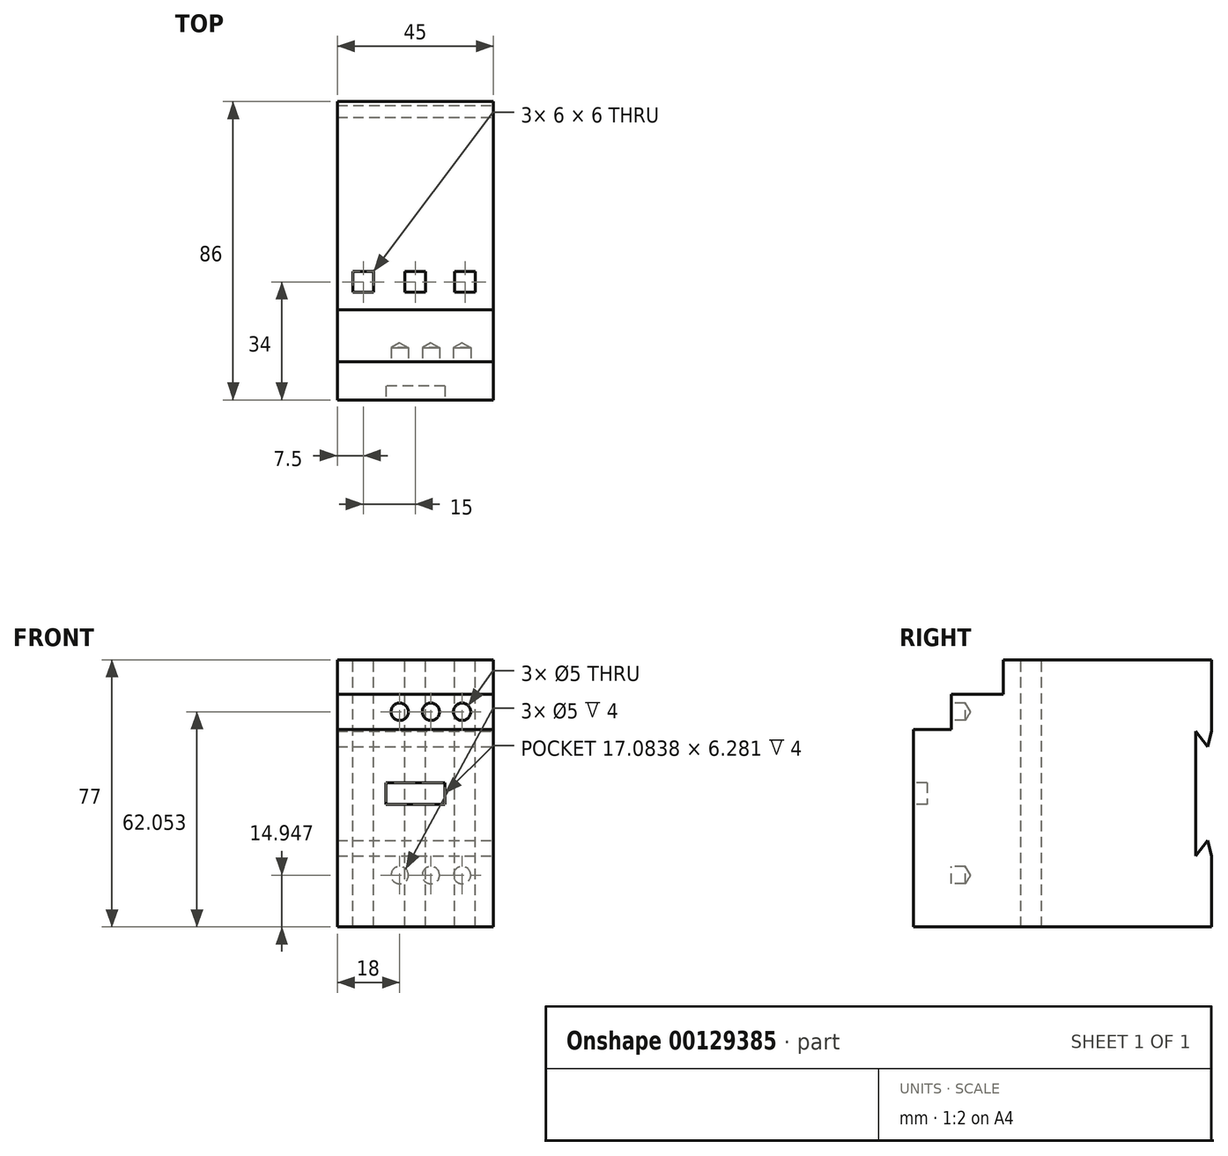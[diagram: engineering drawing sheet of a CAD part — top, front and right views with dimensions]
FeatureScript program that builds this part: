
annotation { "Feature Type Name" : "Feature", "Feature Type Description" : "" }
export const myFeature = defineFeature(function(context is Context, id is Id, definition is map)
    precondition{}
    {
        {
            var Q0;
            Q0=qCreatedBy(makeId("Front.planeOp"),FACE);
            var sketch = newSketch(context, id + "F0", { "sketchPlane" : qUnion([Q0])});
            skLineSegment(sketch, "E0.bottom", {"start": v(22.5, 38.5) * mm, "end": v(-22.5, 38.5) * mm});
            skLineSegment(sketch, "E0.top", {"start": v(22.5, -38.5) * mm, "end": v(-22.5, -38.5) * mm});
            skLineSegment(sketch, "E0.left", {"start": v(22.5, 38.5) * mm, "end": v(22.5, -38.5) * mm});
            skLineSegment(sketch, "E0.right", {"start": v(-22.5, 38.5) * mm, "end": v(-22.5, -38.5) * mm});
            skPoint(sketch, "E0.middle", {"position": v(0, 0) * mm});
            skSolve(sketch);
        }
        {
            var Q0;
            Q0=makeQuery(id+"F0.imprint","IMPRINT",FACE,{"disambiguationData":[TD([[makeQuery(id+"F0.imprint","IMPRINT",EDGE,{"derivedFrom":sQuery(id+"F0.wireOp",EDGE,"E0.bottom")}),1.0]])]});
            extrude(context, id + "F1", {"entities" : qUnion([Q0]), "depth" : 86 * mm});
        }
        {
            var Q0;
            Q0=makeQuery(id+"F1.opExtrude","SWEPT_FACE",FACE,{"disambiguationData":[OSD([sQuery(id+"F0.wireOp",EDGE,"E0.left")])]});
            var sketch = newSketch(context, id + "F2", { "sketchPlane" : qUnion([Q0])});
            skLineSegment(sketch, "E1", {"start": v(-86, 0) * mm, "end": v(-76.93, 0) * mm});
            skLineSegment(sketch, "E2", {"start": v(-86, 18.5) * mm, "end": v(12.72, 18.5) * mm});
            skLineSegment(sketch, "E3.MirrorCS", {"start": v(-86, -18.5) * mm, "end": v(12.72, -18.5) * mm});
            skLineSegment(sketch, "E4", {"start": v(-86, 38.5) * mm, "end": v(-86, -38.5) * mm});
            skPoint(sketch, "E5.orphan", {"position": v(-89.36, 18.5) * mm});
            skPoint(sketch, "E6.orphan", {"position": v(-89.36, -18.5) * mm});
            skLineSegment(sketch, "E7", {"start": v(-86, 38.5) * mm, "end": v(-75, 38.5) * mm});
            skLineSegment(sketch, "E8", {"start": v(-75, 38.5) * mm, "end": v(-75, -38.5) * mm});
            skLineSegment(sketch, "E9", {"start": v(-75, -38.5) * mm, "end": v(-60, -38.5) * mm});
            skLineSegment(sketch, "E10", {"start": v(-60, -38.5) * mm, "end": v(-60, 38.5) * mm});
            skLineSegment(sketch, "E11", {"start": v(-60, 38.5) * mm, "end": v(0, 38.5) * mm});
            skLineSegment(sketch, "E12", {"start": v(-75, 28.6) * mm, "end": v(-60, 28.6) * mm});
            skLineSegment(sketch, "E13.MirrorCS", {"start": v(-75, -28.6) * mm, "end": v(-60, -28.6) * mm});
            skLineSegment(sketch, "E14.bottom", {"start": v(-75, 38.5) * mm, "end": v(-60, 38.5) * mm});
            skLineSegment(sketch, "E14.left", {"start": v(-75, 38.5) * mm, "end": v(-75, 28.6) * mm});
            skLineSegment(sketch, "E14.right", {"start": v(-60, 38.5) * mm, "end": v(-60, 28.6) * mm});
            skLineSegment(sketch, "E15.bottom", {"start": v(-60, -28.6) * mm, "end": v(-75, -28.6) * mm});
            skLineSegment(sketch, "E15.top", {"start": v(-60, -38.5) * mm, "end": v(-75, -38.5) * mm});
            skLineSegment(sketch, "E15.left", {"start": v(-60, -28.6) * mm, "end": v(-60, -38.5) * mm});
            skLineSegment(sketch, "E15.right", {"start": v(-75, -28.6) * mm, "end": v(-75, -38.5) * mm});
            skSolve(sketch);
        }
        {
            var Q0;
            {var subQ4=sQuery(id+"F2.wireOp",EDGE,"E7");Q0=makeQuery(id+"F2.imprint","IMPRINT",FACE,{"disambiguationData":[TD([[makeQuery(id+"F2.imprint","IMPRINT",EDGE,{"derivedFrom":subQ4}),-1.0]])]});}
            var Q1;
            {var subQ0=sQuery(id+"F2.wireOp",EDGE,"E15.right");Q1=makeQuery(id+"F2.imprint","IMPRINT",FACE,{"disambiguationData":[TD([[makeQuery(id+"F2.imprint","IMPRINT",EDGE,{"derivedFrom":subQ0}),-1.0]])]});}
            var Q2;
            Q2=makeQuery(id+"F2.imprint","IMPRINT",FACE,{"disambiguationData":[TD([[makeQuery(id+"F2.imprint","IMPRINT",EDGE,{"derivedFrom":sQuery(id+"F2.wireOp",EDGE,"E14.bottom")}),-1.0]])]});
            var Q3;
            Q3=makeQuery(id+"F2.imprint","IMPRINT",FACE,{"disambiguationData":[TD([[makeQuery(id+"F2.imprint","IMPRINT",EDGE,{"derivedFrom":sQuery(id+"F2.wireOp",EDGE,"E15.bottom")}),1.0]])]});
            extrude(context, id + "F3", {"entities" : qUnion([Q0, Q1, Q2, Q3]), "operationType" : NewBodyOperationType.REMOVE, "oppositeDirection" : true, "depth" : 45 * mm});
        }
        {
            var Q0;
            Q0=makeQuery(id+"F3.boolean.opBoolean","COPY",FACE,{"derivedFrom":makeQuery(id+"F3.opExtrude","SWEPT_FACE",FACE,{"disambiguationData":[OSD([sQuery(id+"F2.wireOp",EDGE,"E12")])]})});
            var sketch = newSketch(context, id + "F4", { "sketchPlane" : qUnion([Q0])});
            skLineSegment(sketch, "E16", {"start": v(-22.5, -67.5) * mm, "end": v(-13.5, -67.5) * mm});
            skLineSegment(sketch, "E17.direction1", {"start": v(-13.5, -67.5) * mm, "end": v(-4.5, -67.5) * mm, "construction": true});
            skLineSegment(sketch, "E18.bottom", {"start": v(-15.75, -69.75) * mm, "end": v(-11.25, -69.75) * mm});
            skLineSegment(sketch, "E18.top", {"start": v(-15.75, -65.25) * mm, "end": v(-11.25, -65.25) * mm});
            skLineSegment(sketch, "E18.left", {"start": v(-15.75, -69.75) * mm, "end": v(-15.75, -65.25) * mm});
            skLineSegment(sketch, "E18.right", {"start": v(-11.25, -69.75) * mm, "end": v(-11.25, -65.25) * mm});
            skPoint(sketch, "E18.middle", {"position": v(-13.5, -67.5) * mm});
            skLineSegment(sketch, "E19.bottom", {"start": v(-6.75, -65.25) * mm, "end": v(-2.25, -65.25) * mm});
            skLineSegment(sketch, "E19.top", {"start": v(-6.75, -69.75) * mm, "end": v(-2.25, -69.75) * mm});
            skLineSegment(sketch, "E19.left", {"start": v(-6.75, -65.25) * mm, "end": v(-6.75, -69.75) * mm});
            skLineSegment(sketch, "E19.right", {"start": v(-2.25, -65.25) * mm, "end": v(-2.25, -69.75) * mm});
            skPoint(sketch, "E19.middle", {"position": v(-4.5, -67.5) * mm});
            skLineSegment(sketch, "E20.bottom", {"start": v(2.25, -65.25) * mm, "end": v(6.75, -65.25) * mm});
            skLineSegment(sketch, "E20.top", {"start": v(2.25, -69.75) * mm, "end": v(6.75, -69.75) * mm});
            skLineSegment(sketch, "E20.left", {"start": v(2.25, -65.25) * mm, "end": v(2.25, -69.75) * mm});
            skLineSegment(sketch, "E20.right", {"start": v(6.75, -65.25) * mm, "end": v(6.75, -69.75) * mm});
            skPoint(sketch, "E20.middle", {"position": v(4.5, -67.5) * mm});
            skLineSegment(sketch, "E21.bottom", {"start": v(11.25, -65.25) * mm, "end": v(15.75, -65.25) * mm});
            skLineSegment(sketch, "E21.top", {"start": v(11.25, -69.75) * mm, "end": v(15.75, -69.75) * mm});
            skLineSegment(sketch, "E21.left", {"start": v(11.25, -65.25) * mm, "end": v(11.25, -69.75) * mm});
            skLineSegment(sketch, "E21.right", {"start": v(15.75, -65.25) * mm, "end": v(15.75, -69.75) * mm});
            skPoint(sketch, "E21.middle", {"position": v(13.5, -67.5) * mm});
            skSolve(sketch);
        }
        {
            var Q0;
            Q0=makeQuery(id+"F1.opExtrude","SWEPT_FACE",FACE,{"disambiguationData":[OSD([sQuery(id+"F0.wireOp",EDGE,"E0.bottom")])]});
            var sketch = newSketch(context, id + "F5", { "sketchPlane" : qUnion([Q0])});
            skLineSegment(sketch, "E22", {"start": v(-22.5, -60) * mm, "end": v(-22.5, -52) * mm});
            skLineSegment(sketch, "E23", {"start": v(-22.5, -52) * mm, "end": v(-15, -52) * mm});
            skPoint(sketch, "E24", {"position": v(-15, -52) * mm});
            skPoint(sketch, "E25.1.0.0", {"position": v(0, -52) * mm});
            skPoint(sketch, "E25.2.0.0", {"position": v(15, -52) * mm});
            skLineSegment(sketch, "E25.direction1", {"start": v(-15, -52) * mm, "end": v(0, -52) * mm, "construction": true});
            skLineSegment(sketch, "E26.bottom", {"start": v(-12, -49) * mm, "end": v(-18, -49) * mm});
            skLineSegment(sketch, "E26.top", {"start": v(-12, -55) * mm, "end": v(-18, -55) * mm});
            skLineSegment(sketch, "E26.left", {"start": v(-12, -49) * mm, "end": v(-12, -55) * mm});
            skLineSegment(sketch, "E26.right", {"start": v(-18, -49) * mm, "end": v(-18, -55) * mm});
            skLineSegment(sketch, "E27.bottom", {"start": v(-3, -49) * mm, "end": v(3, -49) * mm});
            skLineSegment(sketch, "E27.top", {"start": v(-3, -55) * mm, "end": v(3, -55) * mm});
            skLineSegment(sketch, "E27.left", {"start": v(-3, -49) * mm, "end": v(-3, -55) * mm});
            skLineSegment(sketch, "E27.right", {"start": v(3, -49) * mm, "end": v(3, -55) * mm});
            skLineSegment(sketch, "E28.bottom", {"start": v(11.34, -49) * mm, "end": v(17.34, -49) * mm});
            skLineSegment(sketch, "E28.top", {"start": v(11.34, -55) * mm, "end": v(17.34, -55) * mm});
            skLineSegment(sketch, "E28.left", {"start": v(11.34, -49) * mm, "end": v(11.34, -55) * mm});
            skLineSegment(sketch, "E28.right", {"start": v(17.34, -49) * mm, "end": v(17.34, -55) * mm});
            skPoint(sketch, "E28.middle", {"position": v(14.34, -52) * mm});
            skSolve(sketch);
        }
        {
            var Q0;
            {var subQ3=sQuery(id+"F4.wireOp",EDGE,"E18.bottom");Q0=makeQuery(id+"F4.imprint","IMPRINT",FACE,{"disambiguationData":[TD([[makeQuery(id+"F4.imprint","IMPRINT",EDGE,{"derivedFrom":subQ3}),1.0]])]});}
            var Q1;
            Q1=makeQuery(id+"F4.imprint","IMPRINT",FACE,{"disambiguationData":[TD([[makeQuery(id+"F4.imprint","IMPRINT",EDGE,{"derivedFrom":sQuery(id+"F4.wireOp",EDGE,"E19.bottom")}),-1.0]])]});
            var Q2;
            Q2=makeQuery(id+"F4.imprint","IMPRINT",FACE,{"disambiguationData":[TD([[makeQuery(id+"F4.imprint","IMPRINT",EDGE,{"derivedFrom":sQuery(id+"F4.wireOp",EDGE,"E20.bottom")}),-1.0]])]});
            var Q3;
            Q3=makeQuery(id+"F4.imprint","IMPRINT",FACE,{"disambiguationData":[TD([[makeQuery(id+"F4.imprint","IMPRINT",EDGE,{"derivedFrom":sQuery(id+"F4.wireOp",EDGE,"E21.bottom")}),-1.0]])]});
            var Q4;
            {var subQ1=sQuery(id+"F5.wireOp",EDGE,"E26.bottom");Q4=makeQuery(id+"F5.imprint","IMPRINT",FACE,{"disambiguationData":[TD([[makeQuery(id+"F5.imprint","IMPRINT",EDGE,{"derivedFrom":subQ1}),1.0]])]});}
            var Q5;
            Q5=makeQuery(id+"F5.imprint","IMPRINT",FACE,{"disambiguationData":[TD([[makeQuery(id+"F5.imprint","IMPRINT",EDGE,{"derivedFrom":sQuery(id+"F5.wireOp",EDGE,"E27.bottom")}),-1.0]])]});
            var Q6;
            Q6=makeQuery(id+"F5.imprint","IMPRINT",FACE,{"disambiguationData":[TD([[makeQuery(id+"F5.imprint","IMPRINT",EDGE,{"derivedFrom":sQuery(id+"F5.wireOp",EDGE,"E28.bottom")}),-1.0]])]});
            var Q7;
            Q7=makeQuery(id+"F1.opExtrude","SWEPT_FACE",FACE,{"disambiguationData":[OSD([sQuery(id+"F0.wireOp",EDGE,"E0.top")])]});
            extrude(context, id + "F6", {"entities" : qUnion([Q0, Q1, Q2, Q3, Q4, Q5, Q6]), "operationType" : NewBodyOperationType.REMOVE, "endBound" : BoundingType.UP_TO_SURFACE, "oppositeDirection" : true, "endBoundEntityFace" : qUnion([Q7]), "depth" : 10 * mm});
        }
        {
            var Q0;
            Q0=makeQuery(id+"F1.opExtrude","SWEPT_FACE",FACE,{"disambiguationData":[OSD([sQuery(id+"F0.wireOp",EDGE,"E0.left")])]});
            var sketch = newSketch(context, id + "F7", { "sketchPlane" : qUnion([Q0])});
            skLineSegment(sketch, "E29.bottom", {"start": v(4.5, 18) * mm, "end": v(-4.5, 18) * mm});
            skLineSegment(sketch, "E29.top", {"start": v(4.5, -18) * mm, "end": v(-4.5, -18) * mm});
            skLineSegment(sketch, "E29.left", {"start": v(4.5, 18) * mm, "end": v(4.5, -18) * mm});
            skLineSegment(sketch, "E29.right", {"start": v(-4.5, 18) * mm, "end": v(-4.5, -18) * mm});
            skPoint(sketch, "E29.middle", {"position": v(0, 0) * mm});
            skLineSegment(sketch, "E30", {"start": v(-4.5, 18) * mm, "end": v(-1.08, 13.5) * mm});
            skLineSegment(sketch, "E31", {"start": v(-1.08, 13.5) * mm, "end": v(0, 18) * mm});
            skLineSegment(sketch, "E32.MirrorCS", {"start": v(-4.5, -18) * mm, "end": v(-1.08, -13.5) * mm});
            skLineSegment(sketch, "E33.MirrorCS", {"start": v(-1.08, -13.5) * mm, "end": v(0, -18) * mm});
            skSolve(sketch);
        }
        {
            var Q0;
            Q0=makeQuery(id+"F7.imprint","IMPRINT",FACE,{"disambiguationData":[TD([[makeQuery(id+"F7.imprint","IMPRINT",EDGE,{"derivedFrom":sQuery(id+"F7.wireOp",EDGE,"E29.right")}),1.0]])]});
            extrude(context, id + "F8", {"entities" : qUnion([Q0]), "operationType" : NewBodyOperationType.REMOVE, "oppositeDirection" : true, "depth" : 45 * mm});
        }
        {
            var Q0;
            Q0=makeQuery(id+"F1.opExtrude","CAP_FACE",FACE,{"disambiguationData":[OSD([sQuery(id+"F0.wireOp",EDGE,"E0.bottom"),sQuery(id+"F0.wireOp",EDGE,"E0.top"),sQuery(id+"F0.wireOp",EDGE,"E0.left"),sQuery(id+"F0.wireOp",EDGE,"E0.right")])],"isStart":false});
            var sketch = newSketch(context, id + "F9", { "sketchPlane" : qUnion([Q0])});
            skPoint(sketch, "E34", {"position": v(0, 0) * mm});
            skLineSegment(sketch, "E35.bottom", {"start": v(8.54, 3.14) * mm, "end": v(-8.54, 3.14) * mm});
            skLineSegment(sketch, "E35.top", {"start": v(8.54, -3.14) * mm, "end": v(-8.54, -3.14) * mm});
            skLineSegment(sketch, "E35.left", {"start": v(8.54, 3.14) * mm, "end": v(8.54, -3.14) * mm});
            skLineSegment(sketch, "E35.right", {"start": v(-8.54, 3.14) * mm, "end": v(-8.54, -3.14) * mm});
            skSolve(sketch);
        }
        {
            var Q0;
            Q0=makeQuery(id+"F9.imprint","IMPRINT",FACE,{"disambiguationData":[TD([[makeQuery(id+"F9.imprint","IMPRINT",EDGE,{"derivedFrom":sQuery(id+"F9.wireOp",EDGE,"E35.bottom")}),1.0]])]});
            extrude(context, id + "F10", {"entities" : qUnion([Q0]), "operationType" : NewBodyOperationType.REMOVE, "oppositeDirection" : true, "depth" : 4 * mm});
        }
        {
            var Q0;
            {var subQ0=sQuery(id+"F2.wireOp",EDGE,"E8");Q0=makeQuery(id+"F3.boolean.opBoolean","COPY",FACE,{"derivedFrom":makeQuery(id+"F3.opExtrude","SWEPT_FACE",FACE,{"disambiguationData":[OSD([subQ0]),TDD([makeQuery(id+"F2.imprint","IMPRINT",EDGE,{"disambiguationData":[TD([[makeQuery(id+"F2.imprint","INTERSECT",VERTEX,{"derivedFrom":[sQuery(id+"F2.wireOp",EDGE,"E2"),subQ0]}),1.0]])],"derivedFrom":subQ0})])]})});}
            var sketch = newSketch(context, id + "F11", { "sketchPlane" : qUnion([Q0])});
            skPoint(sketch, "E36", {"position": v(-13.5, 23.55) * mm});
            skPoint(sketch, "E36.positionSnap0", {"position": v(-22.5, 23.55) * mm});
            skPoint(sketch, "E37.1.0.0", {"position": v(-4.5, 23.55) * mm});
            skPoint(sketch, "E37.2.0.0", {"position": v(4.5, 23.55) * mm});
            skPoint(sketch, "E37.3.0.0", {"position": v(13.5, 23.55) * mm});
            skLineSegment(sketch, "E37.direction1", {"start": v(-13.5, 23.55) * mm, "end": v(-4.5, 23.55) * mm, "construction": true});
            skSolve(sketch);
        }
        {
            var Q0;
            Q0=makeQuery(id+"F3.boolean.opBoolean","COPY",FACE,{"derivedFrom":makeQuery(id+"F3.opExtrude","SWEPT_FACE",FACE,{"disambiguationData":[OSD([sQuery(id+"F2.wireOp",EDGE,"E14.right")])]})});
            var sketch = newSketch(context, id + "F12", { "sketchPlane" : qUnion([Q0])});
            skPoint(sketch, "E38", {"position": v(-22.5, 33.55) * mm});
            skPoint(sketch, "E39", {"position": v(-15, 33.55) * mm});
            skPoint(sketch, "E40.1.0.0", {"position": v(0, 33.55) * mm});
            skPoint(sketch, "E40.2.0.0", {"position": v(15, 33.55) * mm});
            skLineSegment(sketch, "E40.direction1", {"start": v(-15, 33.55) * mm, "end": v(0, 33.55) * mm, "construction": true});
            skSolve(sketch);
        }
        {
            var Q0;
            {var subQ0=sQuery(id+"F2.wireOp",EDGE,"E8");Q0=makeQuery(id+"F3.boolean.opBoolean","COPY",FACE,{"derivedFrom":makeQuery(id+"F3.opExtrude","SWEPT_FACE",FACE,{"disambiguationData":[OSD([subQ0]),TDD([makeQuery(id+"F2.imprint","IMPRINT",EDGE,{"disambiguationData":[TD([[makeQuery(id+"F2.imprint","INTERSECT",VERTEX,{"derivedFrom":[sQuery(id+"F2.wireOp",EDGE,"E3.MirrorCS"),subQ0]}),-1.0]])],"derivedFrom":subQ0})])]})});}
            var sketch = newSketch(context, id + "F13", { "sketchPlane" : qUnion([Q0])});
            skPoint(sketch, "E41", {"position": v(-13.5, -23.55) * mm});
            skPoint(sketch, "E41.positionSnap0", {"position": v(-22.5, -23.55) * mm});
            skPoint(sketch, "E42.1.0.0", {"position": v(-4.5, -23.55) * mm});
            skPoint(sketch, "E42.2.0.0", {"position": v(4.5, -23.55) * mm});
            skPoint(sketch, "E42.3.0.0", {"position": v(13.5, -23.55) * mm});
            skLineSegment(sketch, "E42.direction1", {"start": v(-13.5, -23.55) * mm, "end": v(-4.5, -23.55) * mm, "construction": true});
            skSolve(sketch);
        }
        {
            var Q0;
            Q0=makeQuery(id+"F3.boolean.opBoolean","COPY",FACE,{"derivedFrom":makeQuery(id+"F3.opExtrude","SWEPT_FACE",FACE,{"disambiguationData":[OSD([sQuery(id+"F2.wireOp",EDGE,"E15.left")])]})});
            var sketch = newSketch(context, id + "F14", { "sketchPlane" : qUnion([Q0])});
            skPoint(sketch, "E43", {"position": v(-15, -33.55) * mm});
            skPoint(sketch, "E43.positionSnap0", {"position": v(-22.5, -33.55) * mm});
            skPoint(sketch, "E44.1.0.0", {"position": v(0, -33.55) * mm});
            skPoint(sketch, "E44.2.0.0", {"position": v(15, -33.55) * mm});
            skLineSegment(sketch, "E44.direction1", {"start": v(-15, -33.55) * mm, "end": v(0, -33.55) * mm, "construction": true});
            skSolve(sketch);
        }
        {
            var Q0;
            Q0=sQuery(id+"F11.wireOp",VERTEX,"E37.1.0.0");
            var Q1;
            Q1=sQuery(id+"F11.wireOp",VERTEX,"E37.2.0.0");
            var Q2;
            Q2=sQuery(id+"F11.wireOp",VERTEX,"E37.3.0.0");
            var Q3;
            Q3=sQuery(id+"F13.wireOp",VERTEX,"E42.1.0.0");
            var Q4;
            Q4=sQuery(id+"F13.wireOp",VERTEX,"E42.2.0.0");
            var Q5;
            Q5=sQuery(id+"F13.wireOp",VERTEX,"E42.3.0.0");
            var Q6;
            Q6=sQuery(id+"F14.wireOp",VERTEX,"E44.2.0.0");
            var Q7;
            Q7=sQuery(id+"F14.wireOp",VERTEX,"E44.1.0.0");
            var Q8;
            Q8=sQuery(id+"F14.wireOp",VERTEX,"E43");
            var Q9;
            Q9=sQuery(id+"F12.wireOp",VERTEX,"E39");
            var Q10;
            Q10=sQuery(id+"F12.wireOp",VERTEX,"E40.1.0.0");
            var Q11;
            Q11=sQuery(id+"F12.wireOp",VERTEX,"E40.2.0.0");
            var Q12;
            Q12=makeQuery(id+"F1.opExtrude","SWEPT_BODY",BODY,{"disambiguationData":[OSD([sQuery(id+"F0.wireOp",EDGE,"E0.bottom"),sQuery(id+"F0.wireOp",EDGE,"E0.top"),sQuery(id+"F0.wireOp",EDGE,"E0.left"),sQuery(id+"F0.wireOp",EDGE,"E0.right")])]});
            hole(context, id + "F15", {"style" : HoleStyle.SIMPLE, "endStyle" : HoleEndStyle.BLIND, "holeDiameter" : 5 * mm, "holeDepth" : 4 * mm, "locations" : qUnion([Q0, Q1, Q2, Q3, Q4, Q5, Q6, Q7, Q8, Q9, Q10, Q11]), "scope" : qUnion([Q12])});
        }
    });
